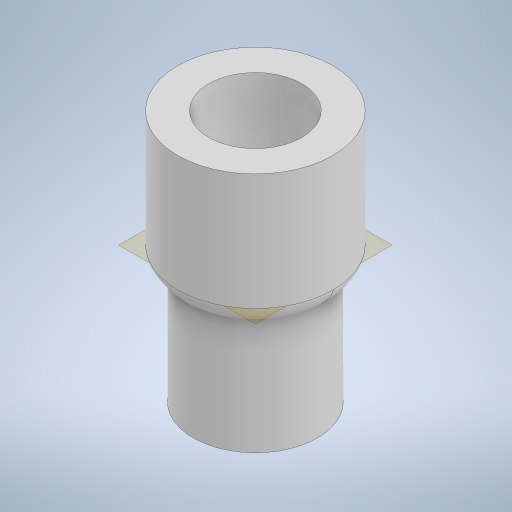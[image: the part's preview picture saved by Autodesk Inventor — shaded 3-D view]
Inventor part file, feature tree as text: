
AUTODESK INVENTOR PART (.ipt)
format: ipt  version: 2024 (Build 280153000, 153)  size: 301,568 bytes
history: native  units: mm
features: other x3, extrude x2, sketch x2, plane x1, loft x1
ambient origin geometry x8: Origin, YZ Plane, XZ Plane, XY Plane, X Axis, Y Axis, Z Axis, Center Point
bodies: Solid1 (feature_tree)
feature tree (9):
  extrude  "Extrusion1"  Depth=10.0mm
  plane  "Work Plane1"
  extrude  "Extrusion2"  Depth=2.5mm
  loft  "Loft1"
  sketch  "Sketch1"  dims[d0=16.0mm d1=10.0mm]
  sketch  "Sketch2"  dims[d2=15.0mm d3=0.0mm d4=2.5mm d5=20.0mm d6=12.0mm d7=15.0mm d8=0.0mm d9=0.0mm d10=90.0deg d11=0.0mm d12=90.0deg d13=0.0mm d14=90.0deg]
  other  "Edges1"
  other  "Edges2"
  other  "Edges3"
